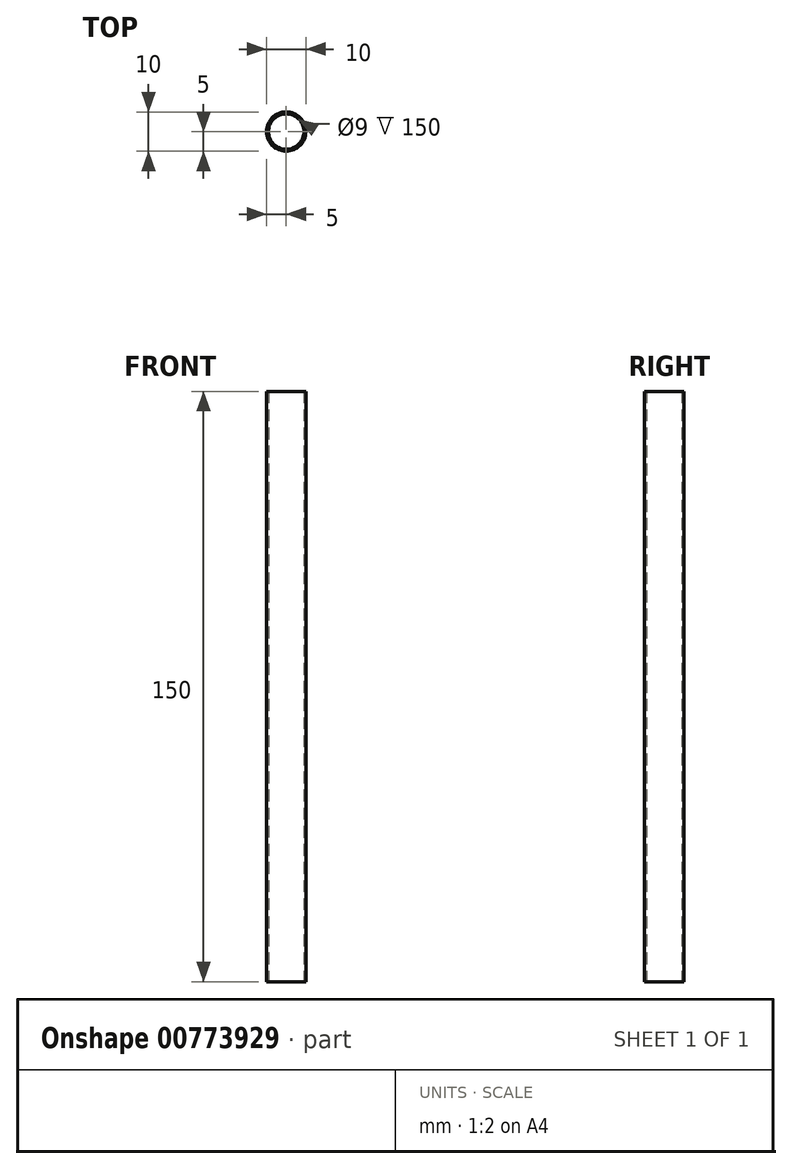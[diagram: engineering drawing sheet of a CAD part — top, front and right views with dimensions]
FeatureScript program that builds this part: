
annotation { "Feature Type Name" : "Feature", "Feature Type Description" : "" }
export const myFeature = defineFeature(function(context is Context, id is Id, definition is map)
    precondition{}
    {
        {
            var Q0;
            Q0=qCreatedBy(makeId("Top.planeOp"),FACE);
            var sketch = newSketch(context, id + "F0", { "sketchPlane" : qUnion([Q0])});
            skCircle(sketch, "E0", {"center": v(0, 0) * mm, "radius": 5 * mm});
            skCircle(sketch, "E1", {"center": v(0, 0) * mm, "radius": 4.5 * mm});
            skSolve(sketch);
        }
        {
            var Q0;
            Q0 = qSketchRegion(id + "F0", true);
            extrude(context, id + "F1", {"entities" : qUnion([Q0]), "depth" : 150 * mm, "offsetDistance" : 25.4 * mm});
        }
    });
